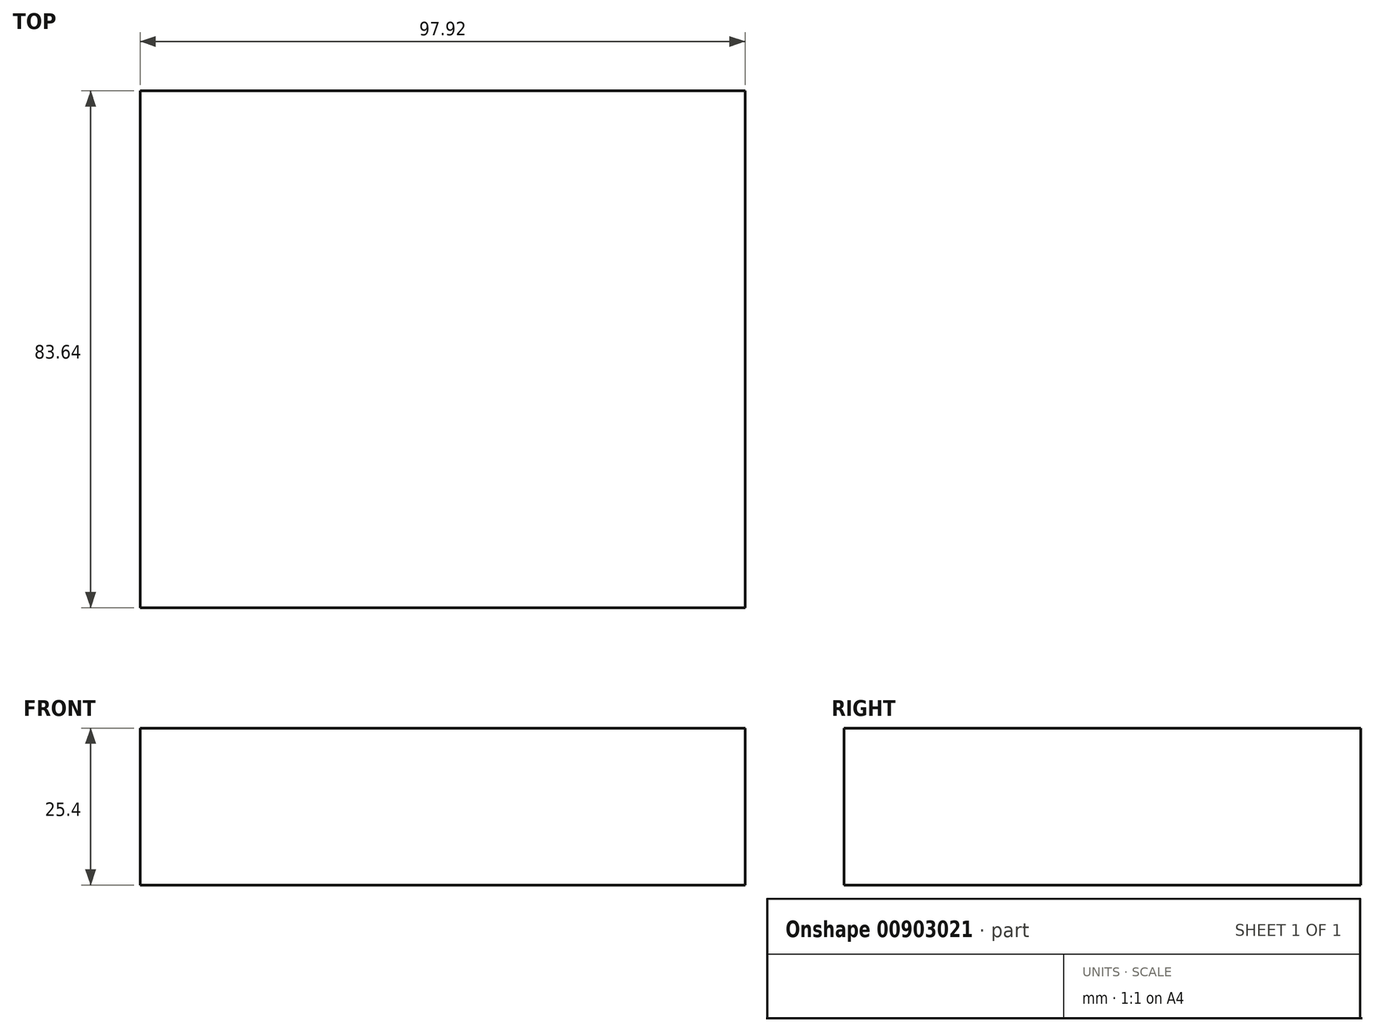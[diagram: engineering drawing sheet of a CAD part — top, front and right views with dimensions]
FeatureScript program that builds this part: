
annotation { "Feature Type Name" : "Feature", "Feature Type Description" : "" }
export const myFeature = defineFeature(function(context is Context, id is Id, definition is map)
    precondition{}
    {
        {
            var Q0;
            Q0=qCreatedBy(makeId("Top.planeOp"),FACE);
            var sketch = newSketch(context, id + "F0", { "sketchPlane" : qUnion([Q0])});
            skLineSegment(sketch, "E0.bottom", {"start": v(48.96, 41.82) * mm, "end": v(-48.96, 41.82) * mm});
            skLineSegment(sketch, "E0.top", {"start": v(48.96, -41.82) * mm, "end": v(-48.96, -41.82) * mm});
            skLineSegment(sketch, "E0.left", {"start": v(48.96, 41.82) * mm, "end": v(48.96, -41.82) * mm});
            skLineSegment(sketch, "E0.right", {"start": v(-48.96, 41.82) * mm, "end": v(-48.96, -41.82) * mm});
            skPoint(sketch, "E0.middle", {"position": v(0, 0) * mm});
            skSolve(sketch);
        }
        {
            var Q0;
            Q0=makeQuery(id+"F0.imprint","IMPRINT",FACE,{"disambiguationData":[TD([[makeQuery(id+"F0.imprint","IMPRINT",EDGE,{"derivedFrom":sQuery(id+"F0.wireOp",EDGE,"E0.bottom")}),1.0]])]});
            extrude(context, id + "F1", {"entities" : qUnion([Q0]), "depth" : 25.4 * mm, "offsetDistance" : 25.4 * mm});
        }
    });
